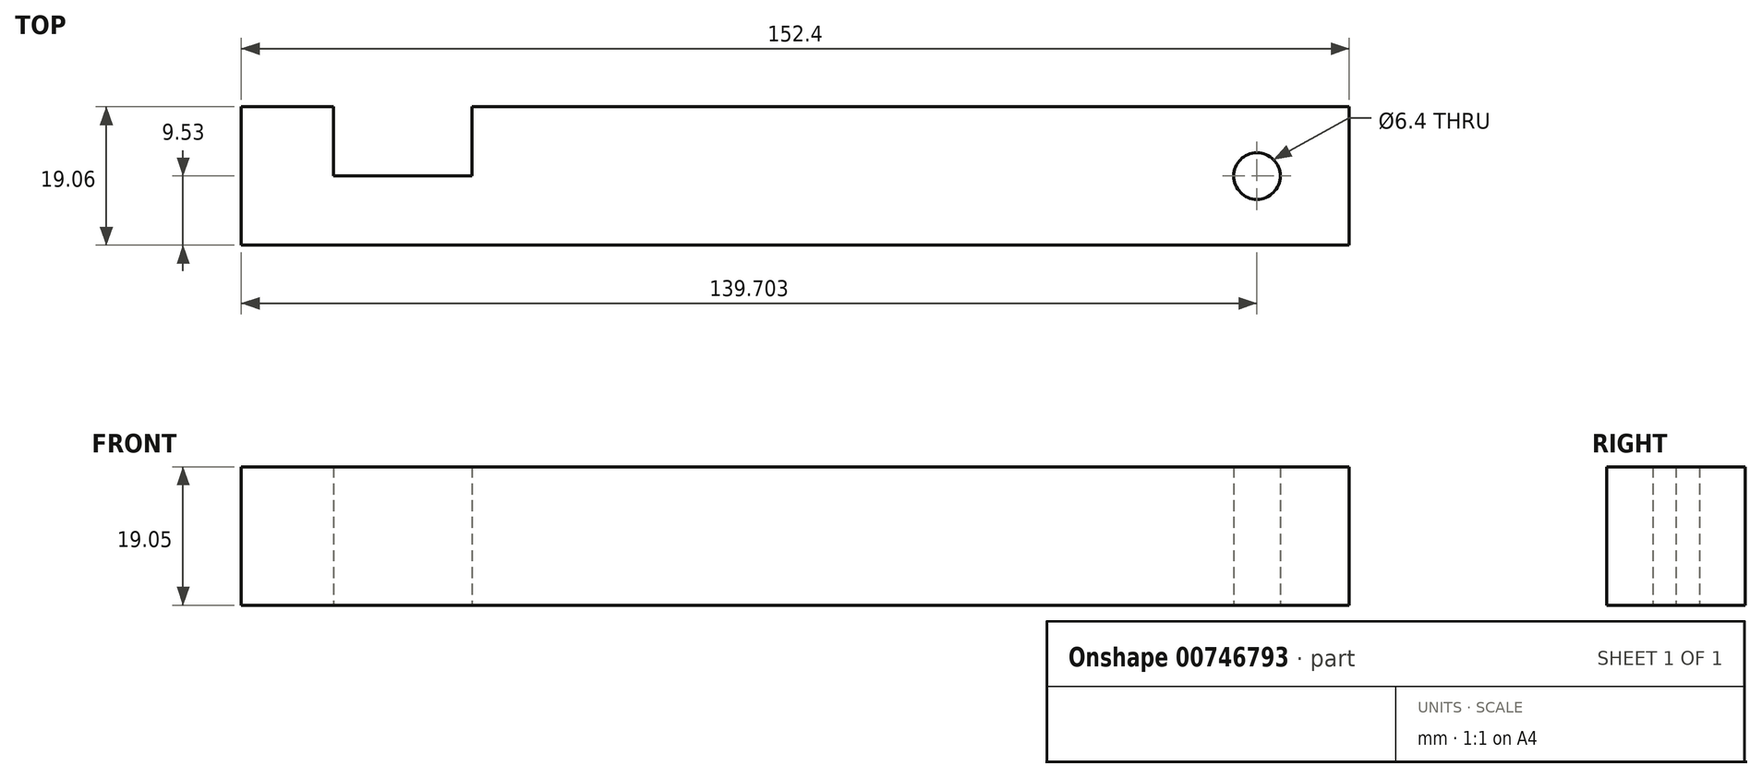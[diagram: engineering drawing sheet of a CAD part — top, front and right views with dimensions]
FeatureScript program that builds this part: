
annotation { "Feature Type Name" : "Feature", "Feature Type Description" : "" }
export const myFeature = defineFeature(function(context is Context, id is Id, definition is map)
    precondition{}
    {
        {
            var Q0;
            Q0=qCreatedBy(makeId("Top.planeOp"),FACE);
            var sketch = newSketch(context, id + "F0", { "sketchPlane" : qUnion([Q0])});
            skLineSegment(sketch, "E0.bottom", {"start": v(-18.67, 9.52) * mm, "end": v(133.73, 9.52) * mm});
            skLineSegment(sketch, "E0.top", {"start": v(-18.67, -9.53) * mm, "end": v(133.73, -9.53) * mm});
            skLineSegment(sketch, "E0.left", {"start": v(-18.67, 9.52) * mm, "end": v(-18.67, -9.53) * mm});
            skLineSegment(sketch, "E0.right", {"start": v(133.73, 9.52) * mm, "end": v(133.73, -9.53) * mm});
            skLineSegment(sketch, "E1.bottom", {"start": v(-5.97, 9.52) * mm, "end": v(13.08, 9.52) * mm});
            skLineSegment(sketch, "E1.top", {"start": v(-5.97, 0) * mm, "end": v(13.08, 0) * mm});
            skLineSegment(sketch, "E1.left", {"start": v(-5.97, 9.52) * mm, "end": v(-5.97, 0) * mm});
            skLineSegment(sketch, "E1.right", {"start": v(13.08, 9.52) * mm, "end": v(13.08, 0) * mm});
            skCircle(sketch, "E2", {"center": v(121.03, 0) * mm, "radius": 3.2 * mm});
            skSolve(sketch);
        }
        {
            var Q0;
            Q0=makeQuery(id+"F0.imprint","IMPRINT",FACE,{"disambiguationData":[TD([[makeQuery(id+"F0.imprint","IMPRINT",EDGE,{"derivedFrom":sQuery(id+"F0.wireOp",EDGE,"E0.top")}),1.0]])]});
            extrude(context, id + "F1", {"entities" : qUnion([Q0]), "depth" : 19.05 * mm, "offsetDistance" : 25.4 * mm});
        }
    });
